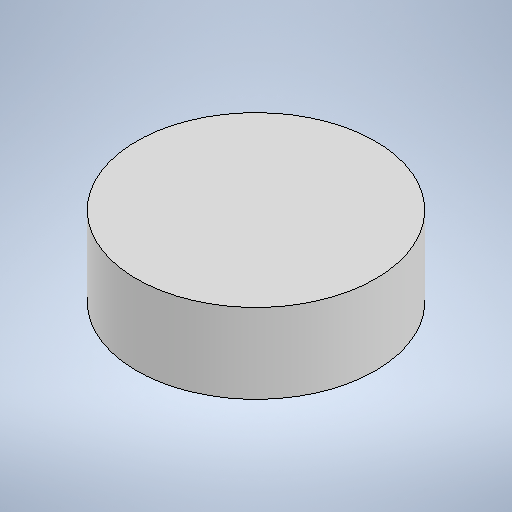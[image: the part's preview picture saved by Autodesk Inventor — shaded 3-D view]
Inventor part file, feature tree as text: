
AUTODESK INVENTOR PART (.ipt)
format: ipt  version: 2025.1 (Build 291241020, 241B)  size: 345,600 bytes
history: native  units: mm
features: sketch x8, extrude x1, revolve x1
ambient origin geometry x8: Origin, YZ Plane, XZ Plane, XY Plane, X Axis, Y Axis, Z Axis, Center Point
bodies: Solid1 (feature_tree)
feature tree (10):
  sketch  "Sketch1"  dims[d0=88.9mm d1=3.0mm]
  sketch  "Sketch2"  dims[d7=120.0mm d9=360.0deg]
  extrude  "Extrusion1"  Depth=3.0mm
  revolve  "Revolution1"  Angle=360.0deg
  sketch  "Sketch Circular Pattern1"  dims[d2=1200.0mm d3=120.0mm d5=360.0deg]
  sketch  "Sketch Circular Pattern2"  dims[d11=200.0mm]
  sketch  "Sketch Circular Pattern3"  dims[d12=120.0mm d14=360.0deg]
  sketch  "Sketch Circular Pattern4"  dims[d20=15.0deg]
  sketch  "Sketch3"  dims[d16=40.0mm d18=360.0deg]
  sketch  "Sketch4"  dims[d21=0.0mm d22=15.0deg d23=45.0deg d24=140.0mm d25=300.0mm d26=460.0mm d27=560.0mm d28=30.0mm d29=10.0mm d30=0.0mm d31=6.0mm d32=1803.421613mm d33=1200.0mm d37=100.0mm d38=30.0mm d39=1200.0mm d40=6.0mm d41=1200.0mm d42=253.289193mm d43=90.0deg]
